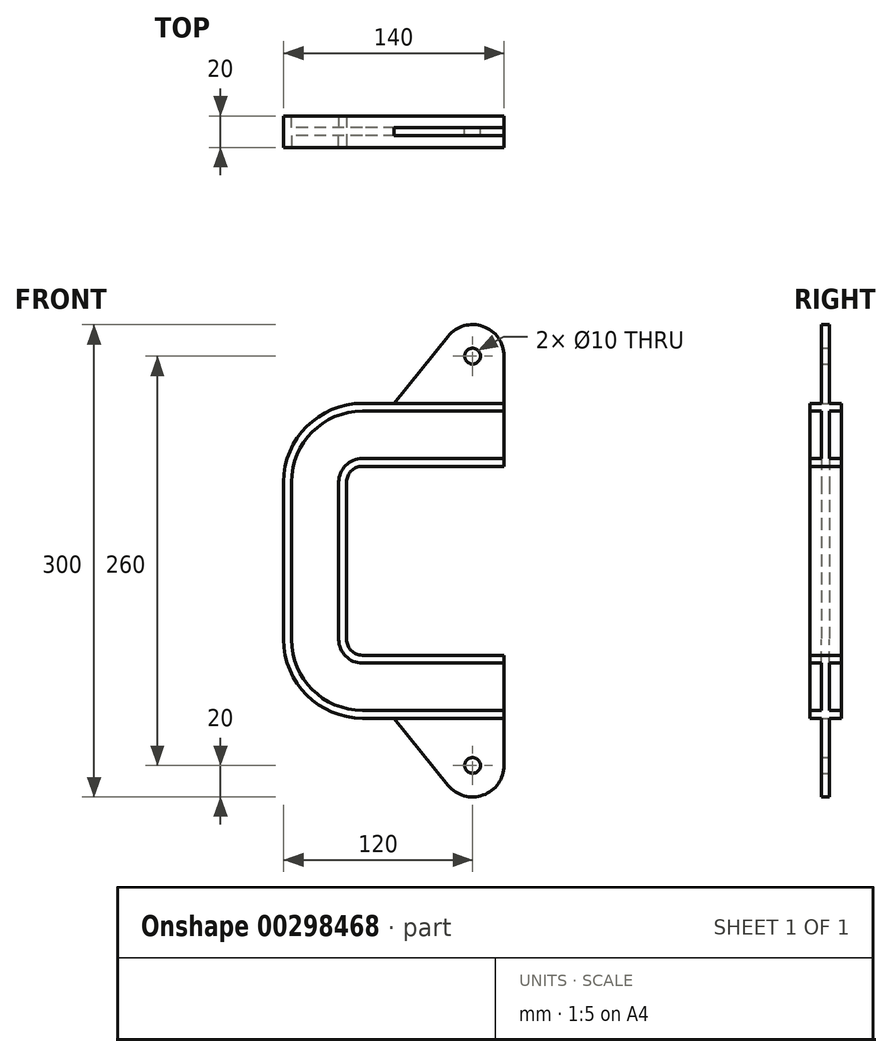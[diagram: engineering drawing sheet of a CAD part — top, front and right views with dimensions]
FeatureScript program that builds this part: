
annotation { "Feature Type Name" : "Feature", "Feature Type Description" : "" }
export const myFeature = defineFeature(function(context is Context, id is Id, definition is map)
    precondition{}
    {
        {
            var Q0;
            Q0=qCreatedBy(makeId("Front.planeOp"),FACE);
            var sketch = newSketch(context, id + "F0", { "sketchPlane" : qUnion([Q0])});
            skLineSegment(sketch, "E0", {"start": v(0, 60) * mm, "end": v(-90, 60) * mm});
            skLineSegment(sketch, "E1", {"start": v(-100, 50) * mm, "end": v(-100, 0) * mm});
            skPoint(sketch, "E2.visualSharp", {"position": v(-100, 60) * mm});
            skArc(sketch, "E2.filletArc", {"start": v(-90, 60) * mm, "mid": v(-97.07, 57.07) * mm, "end": v(-100, 50) * mm});
            skSolve(sketch);
        }
        {
            var Q0;
            Q0=qCreatedBy(makeId("Right.planeOp"),FACE);
            var sketch = newSketch(context, id + "F1", { "sketchPlane" : qUnion([Q0])});
            skLineSegment(sketch, "E3", {"start": v(0, 60) * mm, "end": v(-10, 60) * mm});
            skLineSegment(sketch, "E4", {"start": v(-10, 60) * mm, "end": v(-10, 65) * mm});
            skLineSegment(sketch, "E5", {"start": v(-10, 65) * mm, "end": v(-2.5, 65) * mm});
            skLineSegment(sketch, "E6", {"start": v(-2.5, 65) * mm, "end": v(-2.5, 95) * mm});
            skLineSegment(sketch, "E7", {"start": v(-2.5, 95) * mm, "end": v(-10, 95) * mm});
            skLineSegment(sketch, "E8", {"start": v(-10, 95) * mm, "end": v(-10, 100) * mm});
            skLineSegment(sketch, "E9", {"start": v(-10, 100) * mm, "end": v(0, 100) * mm});
            skLineSegment(sketch, "E10.MirrorCS", {"start": v(10, 60) * mm, "end": v(10, 65) * mm});
            skLineSegment(sketch, "E11.MirrorCS", {"start": v(10, 95) * mm, "end": v(10, 100) * mm});
            skLineSegment(sketch, "E12.MirrorCS", {"start": v(2.5, 95) * mm, "end": v(10, 95) * mm});
            skLineSegment(sketch, "E13.MirrorCS", {"start": v(2.5, 65) * mm, "end": v(2.5, 95) * mm});
            skLineSegment(sketch, "E14.MirrorCS", {"start": v(10, 65) * mm, "end": v(2.5, 65) * mm});
            skLineSegment(sketch, "E15.MirrorCS", {"start": v(0, 60) * mm, "end": v(10, 60) * mm});
            skLineSegment(sketch, "E16.MirrorCS", {"start": v(10, 100) * mm, "end": v(0, 100) * mm});
            skSolve(sketch);
        }
        {
            var Q0;
            Q0=makeQuery(id+"F1.imprint","IMPRINT",FACE,{"disambiguationData":[TD([[makeQuery(id+"F1.imprint","IMPRINT",EDGE,{"derivedFrom":sQuery(id+"F1.wireOp",EDGE,"E3")}),-1.0]])]});
            var Q1;
            Q1=sQuery(id+"F0.wireOp",EDGE,"E0");
            var Q2;
            Q2=sQuery(id+"F0.wireOp",EDGE,"E2.filletArc");
            var Q3;
            Q3=sQuery(id+"F0.wireOp",EDGE,"E1");
            sweep(context, id + "F2", {"profiles" : qUnion([Q0]), "path" : qUnion([Q1, Q2, Q3])});
        }
        {
            var Q0;
            Q0=makeQuery(id+"F2.opSweep","SWEPT_BODY",BODY,{"disambiguationData":[OSD([sQuery(id+"F0.wireOp",EDGE,"E1"),sQuery(id+"F1.wireOp",EDGE,"E3"),sQuery(id+"F1.wireOp",EDGE,"E4"),sQuery(id+"F1.wireOp",EDGE,"E5"),sQuery(id+"F1.wireOp",EDGE,"E6"),sQuery(id+"F1.wireOp",EDGE,"E7"),sQuery(id+"F1.wireOp",EDGE,"E8"),sQuery(id+"F1.wireOp",EDGE,"E9"),sQuery(id+"F1.wireOp",EDGE,"E10.MirrorCS"),sQuery(id+"F1.wireOp",EDGE,"E11.MirrorCS"),sQuery(id+"F1.wireOp",EDGE,"E12.MirrorCS"),sQuery(id+"F1.wireOp",EDGE,"E13.MirrorCS"),sQuery(id+"F1.wireOp",EDGE,"E14.MirrorCS"),sQuery(id+"F1.wireOp",EDGE,"E15.MirrorCS"),sQuery(id+"F1.wireOp",EDGE,"E16.MirrorCS")])]});
            var Q1;
            Q1=qCreatedBy(makeId("Top.planeOp"),FACE);
            mirror(context, id + "F3", {"operationType" : NewBodyOperationType.ADD, "entities" : qUnion([Q0]), "mirrorPlane" : qUnion([Q1])});
        }
        {
            var Q0;
            Q0=qCreatedBy(makeId("Front.planeOp"),FACE);
            var sketch = newSketch(context, id + "F4", { "sketchPlane" : qUnion([Q0])});
            skLineSegment(sketch, "E17", {"start": v(0, 100) * mm, "end": v(0, 130) * mm});
            skLineSegment(sketch, "E18", {"start": v(-35.55, 142.58) * mm, "end": v(-70, 100) * mm});
            skLineSegment(sketch, "E19", {"start": v(-70, 100) * mm, "end": v(0, 100) * mm});
            skPoint(sketch, "E20.visualSharp", {"position": v(0, 186.51) * mm});
            skArc(sketch, "E20.filletArc", {"start": v(0, 130) * mm, "mid": v(-13.33, 148.85) * mm, "end": v(-35.55, 142.58) * mm});
            skCircle(sketch, "E21", {"center": v(-20, 130) * mm, "radius": 5 * mm});
            skSolve(sketch);
        }
        {
            var Q0;
            Q0 = qSketchRegion(id + "F4", true);
            extrude(context, id + "F5", {"entities" : qUnion([Q0]), "operationType" : NewBodyOperationType.ADD, "endBound" : BoundingType.SYMMETRIC, "depth" : 5 * mm});
        }
        {
            var Q0;
            Q0=makeQuery(id+"F2.opSweep","SWEPT_BODY",BODY,{"disambiguationData":[OSD([sQuery(id+"F0.wireOp",EDGE,"E1"),sQuery(id+"F1.wireOp",EDGE,"E3"),sQuery(id+"F1.wireOp",EDGE,"E4"),sQuery(id+"F1.wireOp",EDGE,"E5"),sQuery(id+"F1.wireOp",EDGE,"E6"),sQuery(id+"F1.wireOp",EDGE,"E7"),sQuery(id+"F1.wireOp",EDGE,"E8"),sQuery(id+"F1.wireOp",EDGE,"E9"),sQuery(id+"F1.wireOp",EDGE,"E10.MirrorCS"),sQuery(id+"F1.wireOp",EDGE,"E11.MirrorCS"),sQuery(id+"F1.wireOp",EDGE,"E12.MirrorCS"),sQuery(id+"F1.wireOp",EDGE,"E13.MirrorCS"),sQuery(id+"F1.wireOp",EDGE,"E14.MirrorCS"),sQuery(id+"F1.wireOp",EDGE,"E15.MirrorCS"),sQuery(id+"F1.wireOp",EDGE,"E16.MirrorCS")])]});
            var Q1;
            Q1=qCreatedBy(makeId("Top.planeOp"),FACE);
            mirror(context, id + "F6", {"operationType" : NewBodyOperationType.ADD, "entities" : qUnion([Q0]), "mirrorPlane" : qUnion([Q1])});
        }
    });
